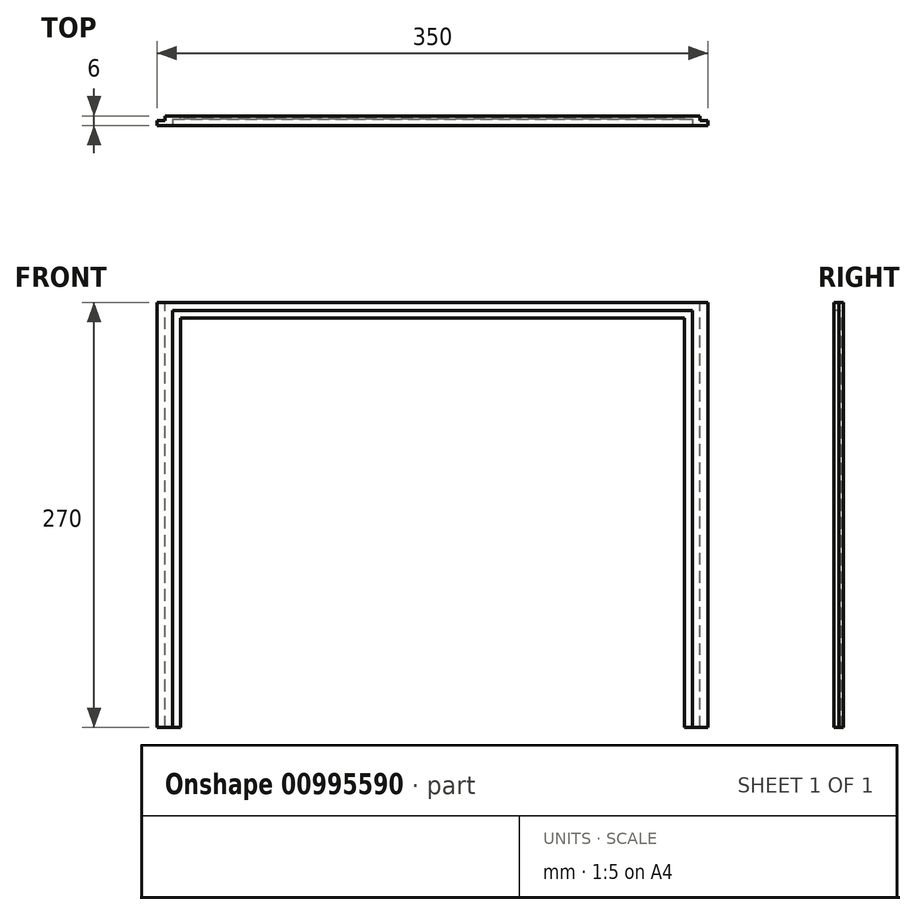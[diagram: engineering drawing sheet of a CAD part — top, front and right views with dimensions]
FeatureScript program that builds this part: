
annotation { "Feature Type Name" : "Feature", "Feature Type Description" : "" }
export const myFeature = defineFeature(function(context is Context, id is Id, definition is map)
    precondition{}
    {
        {
            var Q0;
            Q0=qCreatedBy(makeId("Front.planeOp"),FACE);
            var sketch = newSketch(context, id + "F0", { "sketchPlane" : qUnion([Q0])});
            skLineSegment(sketch, "E0", {"start": v(0, 0) * mm, "end": v(0, 270) * mm});
            skLineSegment(sketch, "E1", {"start": v(0, 270) * mm, "end": v(340, 270) * mm});
            skLineSegment(sketch, "E2", {"start": v(340, 270) * mm, "end": v(340, 0) * mm});
            skLineSegment(sketch, "E3", {"start": v(340, 0) * mm, "end": v(330, 0) * mm});
            skLineSegment(sketch, "E4", {"start": v(330, 0) * mm, "end": v(330, 260) * mm});
            skLineSegment(sketch, "E5", {"start": v(330, 260) * mm, "end": v(10, 260) * mm});
            skLineSegment(sketch, "E6", {"start": v(10, 260) * mm, "end": v(10, 0) * mm});
            skLineSegment(sketch, "E7", {"start": v(10, 0) * mm, "end": v(0, 0) * mm});
            skSolve(sketch);
        }
        {
            var Q0;
            Q0 = qSketchRegion(id + "F0", true);
            extrude(context, id + "F1", {"entities" : qUnion([Q0]), "depth" : 6 * mm, "offsetDistance" : 25 * mm});
        }
        {
            var Q0;
            Q0=makeQuery(id+"F1.opExtrude","CAP_FACE",FACE,{"disambiguationData":[OSD([sQuery(id+"F0.wireOp",EDGE,"E0"),sQuery(id+"F0.wireOp",EDGE,"E1"),sQuery(id+"F0.wireOp",EDGE,"E2"),sQuery(id+"F0.wireOp",EDGE,"E3"),sQuery(id+"F0.wireOp",EDGE,"E4"),sQuery(id+"F0.wireOp",EDGE,"E5"),sQuery(id+"F0.wireOp",EDGE,"E6"),sQuery(id+"F0.wireOp",EDGE,"E7")])],"isStart":false});
            var sketch = newSketch(context, id + "F2", { "sketchPlane" : qUnion([Q0])});
            skPoint(sketch, "E8.oppositeSnap0", {"position": v(335, 0) * mm});
            skLineSegment(sketch, "E8.bottom", {"start": v(5, 0) * mm, "end": v(335, 0) * mm});
            skLineSegment(sketch, "E8.top", {"start": v(5, 265) * mm, "end": v(335, 265) * mm});
            skLineSegment(sketch, "E8.left", {"start": v(5, 0) * mm, "end": v(5, 265) * mm});
            skLineSegment(sketch, "E8.right", {"start": v(335, 0) * mm, "end": v(335, 265) * mm});
            skSolve(sketch);
        }
        {
            var Q0;
            Q0 = qSketchRegion(id + "F2", true);
            extrude(context, id + "F3", {"entities" : qUnion([Q0]), "operationType" : NewBodyOperationType.REMOVE, "oppositeDirection" : true, "depth" : 4 * mm, "offsetDistance" : 25 * mm});
        }
        {
            var Q0;
            Q0=makeQuery(id+"F1.opExtrude","SWEPT_FACE",FACE,{"disambiguationData":[OSD([sQuery(id+"F0.wireOp",EDGE,"E0")])]});
            var sketch = newSketch(context, id + "F4", { "sketchPlane" : qUnion([Q0])});
            skLineSegment(sketch, "E9.bottom", {"start": v(6, 0) * mm, "end": v(3, 0) * mm});
            skLineSegment(sketch, "E9.top", {"start": v(6, 270) * mm, "end": v(3, 270) * mm});
            skLineSegment(sketch, "E9.left", {"start": v(6, 0) * mm, "end": v(6, 270) * mm});
            skLineSegment(sketch, "E9.right", {"start": v(3, 0) * mm, "end": v(3, 270) * mm});
            skSolve(sketch);
        }
        {
            var Q0;
            Q0 = qSketchRegion(id + "F4", true);
            extrude(context, id + "F5", {"entities" : qUnion([Q0]), "operationType" : NewBodyOperationType.ADD, "depth" : 5 * mm, "offsetDistance" : 25 * mm});
        }
        {
            var Q0;
            Q0=makeQuery(id+"F1.opExtrude","SWEPT_FACE",FACE,{"disambiguationData":[OSD([sQuery(id+"F0.wireOp",EDGE,"E2")])]});
            var sketch = newSketch(context, id + "F6", { "sketchPlane" : qUnion([Q0])});
            skLineSegment(sketch, "E10.bottom", {"start": v(-6, 0) * mm, "end": v(-3, 0) * mm});
            skLineSegment(sketch, "E10.top", {"start": v(-6, 270) * mm, "end": v(-3, 270) * mm});
            skLineSegment(sketch, "E10.left", {"start": v(-6, 0) * mm, "end": v(-6, 270) * mm});
            skLineSegment(sketch, "E10.right", {"start": v(-3, 0) * mm, "end": v(-3, 270) * mm});
            skSolve(sketch);
        }
        {
            var Q0;
            Q0 = qSketchRegion(id + "F6", true);
            extrude(context, id + "F7", {"entities" : qUnion([Q0]), "operationType" : NewBodyOperationType.ADD, "depth" : 5 * mm, "offsetDistance" : 25 * mm});
        }
    });
